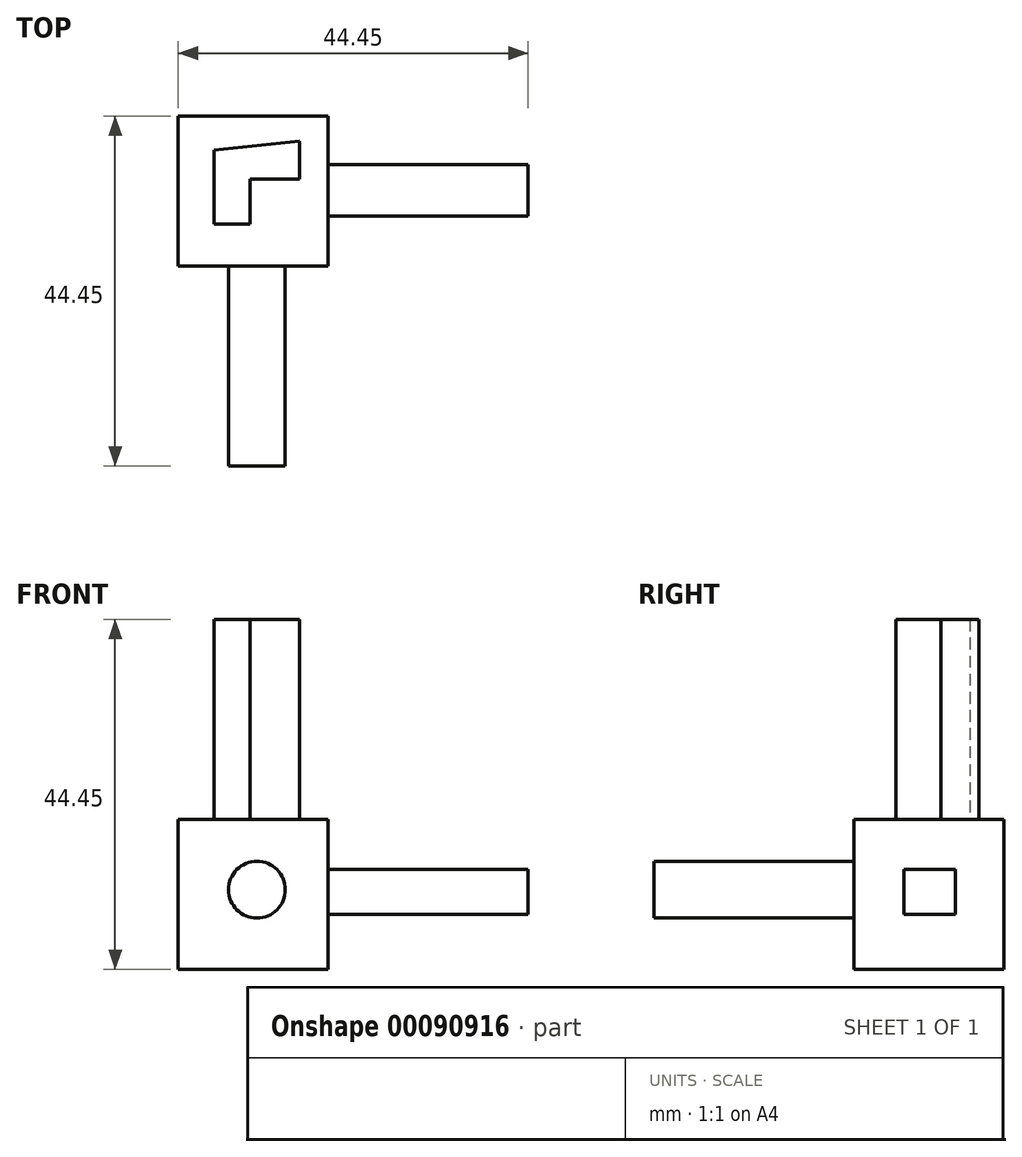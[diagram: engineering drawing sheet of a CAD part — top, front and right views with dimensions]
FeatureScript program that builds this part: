
annotation { "Feature Type Name" : "Feature", "Feature Type Description" : "" }
export const myFeature = defineFeature(function(context is Context, id is Id, definition is map)
    precondition{}
    {
        {
            var Q0;
            Q0=qCreatedBy(makeId("Top.planeOp"),FACE);
            var sketch = newSketch(context, id + "F0", { "sketchPlane" : qUnion([Q0])});
            skLineSegment(sketch, "E0.bottom", {"start": v(-28.25, 19) * mm, "end": v(-9.2, 19) * mm});
            skLineSegment(sketch, "E0.top", {"start": v(-28.25, -0.05) * mm, "end": v(-9.2, -0.05) * mm});
            skLineSegment(sketch, "E0.left", {"start": v(-28.25, 19) * mm, "end": v(-28.25, -0.05) * mm});
            skLineSegment(sketch, "E0.right", {"start": v(-9.2, 19) * mm, "end": v(-9.2, -0.05) * mm});
            skSolve(sketch);
        }
        {
            var Q0;
            Q0=makeQuery(id+"F0.imprint","IMPRINT",FACE,{"disambiguationData":[TD([[makeQuery(id+"F0.imprint","IMPRINT",EDGE,{"derivedFrom":sQuery(id+"F0.wireOp",EDGE,"E0.bottom")}),-1.0]])]});
            extrude(context, id + "F1", {"entities" : qUnion([Q0]), "depth" : 19.05 * mm});
        }
        {
            var Q0;
            Q0=makeQuery(id+"F1.opExtrude","SWEPT_FACE",FACE,{"disambiguationData":[OSD([sQuery(id+"F0.wireOp",EDGE,"E0.top")])]});
            var sketch = newSketch(context, id + "F2", { "sketchPlane" : qUnion([Q0])});
            skCircle(sketch, "E1", {"center": v(-18.26, 10.13) * mm, "radius": 3.6 * mm});
            skSolve(sketch);
        }
        {
            var Q0;
            Q0=makeQuery(id+"F2.imprint","IMPRINT",FACE,{"disambiguationData":[TD([[makeQuery(id+"F2.imprint","IMPRINT",EDGE,{"derivedFrom":sQuery(id+"F2.wireOp",EDGE,"E1")}),1.0]])]});
            extrude(context, id + "F3", {"entities" : qUnion([Q0]), "operationType" : NewBodyOperationType.ADD, "depth" : 25.4 * mm});
        }
        {
            var Q0;
            Q0=makeQuery(id+"F1.opExtrude","SWEPT_FACE",FACE,{"disambiguationData":[OSD([sQuery(id+"F0.wireOp",EDGE,"E0.right")])]});
            var sketch = newSketch(context, id + "F4", { "sketchPlane" : qUnion([Q0])});
            skLineSegment(sketch, "E2.bottom", {"start": v(6.28, 12.7) * mm, "end": v(12.84, 12.7) * mm});
            skLineSegment(sketch, "E2.top", {"start": v(6.28, 6.99) * mm, "end": v(12.84, 6.99) * mm});
            skLineSegment(sketch, "E2.left", {"start": v(6.28, 12.7) * mm, "end": v(6.28, 6.99) * mm});
            skLineSegment(sketch, "E2.right", {"start": v(12.84, 12.7) * mm, "end": v(12.84, 6.99) * mm});
            skSolve(sketch);
        }
        {
            var Q0;
            Q0=makeQuery(id+"F4.imprint","IMPRINT",FACE,{"disambiguationData":[TD([[makeQuery(id+"F4.imprint","IMPRINT",EDGE,{"derivedFrom":sQuery(id+"F4.wireOp",EDGE,"E2.bottom")}),-1.0]])]});
            extrude(context, id + "F5", {"entities" : qUnion([Q0]), "operationType" : NewBodyOperationType.ADD, "depth" : 25.4 * mm});
        }
        {
            var Q0;
            Q0=makeQuery(id+"F1.opExtrude","CAP_FACE",FACE,{"disambiguationData":[OSD([sQuery(id+"F0.wireOp",EDGE,"E0.bottom"),sQuery(id+"F0.wireOp",EDGE,"E0.top"),sQuery(id+"F0.wireOp",EDGE,"E0.left"),sQuery(id+"F0.wireOp",EDGE,"E0.right")])],"isStart":false});
            var sketch = newSketch(context, id + "F6", { "sketchPlane" : qUnion([Q0])});
            skLineSegment(sketch, "E3", {"start": v(-23.67, 14.69) * mm, "end": v(-23.67, 5.28) * mm});
            skLineSegment(sketch, "E4", {"start": v(-23.67, 5.28) * mm, "end": v(-19.11, 5.28) * mm});
            skLineSegment(sketch, "E5", {"start": v(-19.11, 5.28) * mm, "end": v(-19.11, 10.98) * mm});
            skLineSegment(sketch, "E6", {"start": v(-19.11, 10.98) * mm, "end": v(-12.84, 10.98) * mm});
            skLineSegment(sketch, "E7", {"start": v(-12.84, 10.98) * mm, "end": v(-12.84, 15.83) * mm});
            skLineSegment(sketch, "E8", {"start": v(-12.84, 15.83) * mm, "end": v(-23.67, 14.69) * mm});
            skSolve(sketch);
        }
        {
            var Q0;
            Q0=makeQuery(id+"F6.imprint","IMPRINT",FACE,{"disambiguationData":[TD([[makeQuery(id+"F6.imprint","IMPRINT",EDGE,{"derivedFrom":sQuery(id+"F6.wireOp",EDGE,"E3")}),1.0]])]});
            extrude(context, id + "F7", {"entities" : qUnion([Q0]), "operationType" : NewBodyOperationType.ADD, "depth" : 25.4 * mm});
        }
    });
